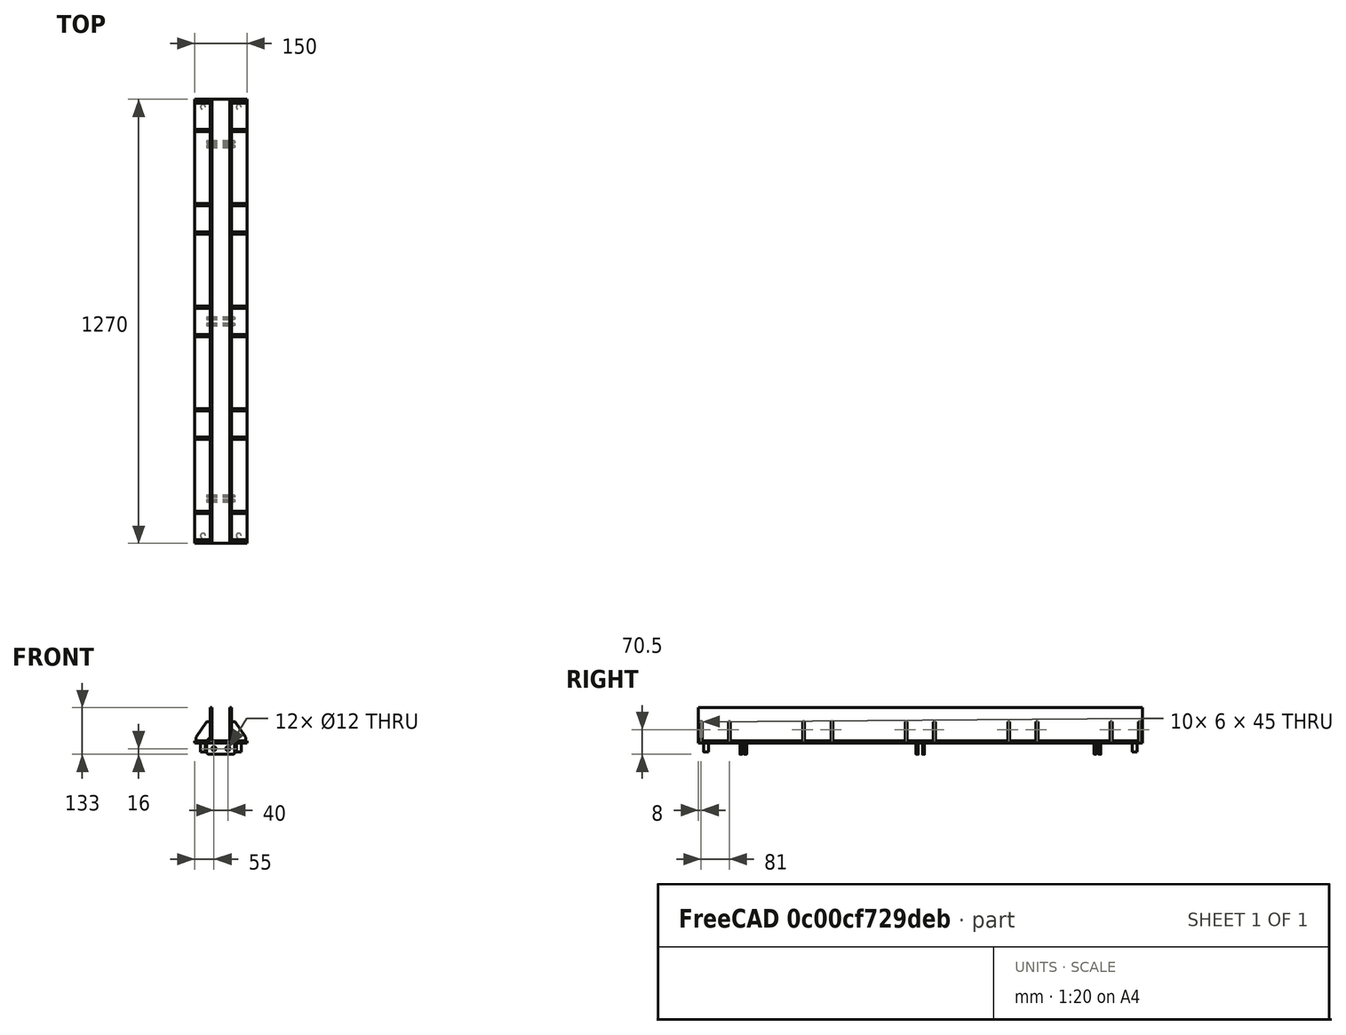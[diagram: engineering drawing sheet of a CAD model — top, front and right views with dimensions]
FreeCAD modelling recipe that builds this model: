
FCSTD DOCUMENT  (FreeCAD 0.21R33771 (Git))
Label: Transom 1270_95_20kN_load
License: All rights reserved
LicenseURL: https://en.wikipedia.org/wiki/All_rights_reserved
objects: Part::FeaturePython×12, Sketcher::SketchObject×3, Fem::ConstraintDisplacement×2, PartDesign::Pad×1, PartDesign::Body×1, Part::Cylinder×1, Part::Compound×1, App::MaterialObjectPython×1, Fem::FemSolverObjectPython×1, Part::MultiFuse×1, Fem::ConstraintForce×1, Fem::FemMeshObjectPython×1, Fem::FemAnalysis×1
note: 19 computed .brp shape members not serialized (recipe doc carries the construction recipe); baked Part::Feature solids carry a one-line shape summary decoded from their .brp

FEATURE [Sketcher::SketchObject] Sketch
  FullyConstrained = true
  MapMode = 5
  Placement = pos=(0,0,0) rot=(1,0,0;1.5708rad)
  sketch-geometry (14):
    g0: LineSegment StartX=0 StartY=0 StartZ=0 EndX=75 EndY=0 EndZ=0
    g1: LineSegment StartX=75 StartY=0 StartZ=0 EndX=75 EndY=6 EndZ=0
    g2: LineSegment StartX=75 StartY=6 StartZ=0 EndX=31 EndY=6 EndZ=0
    g3: LineSegment StartX=31 StartY=6 StartZ=0 EndX=31 EndY=101 EndZ=0
    g4: LineSegment StartX=31 StartY=101 StartZ=0 EndX=25 EndY=101 EndZ=0
    g5: LineSegment StartX=25 StartY=101 StartZ=0 EndX=25 EndY=6 EndZ=0
    g6: LineSegment StartX=25 StartY=6 StartZ=0 EndX=0 EndY=6 EndZ=0
    g7: LineSegment StartX=0 StartY=6 StartZ=0 EndX=-25 EndY=6 EndZ=0
    g8: LineSegment StartX=-25 StartY=6 StartZ=0 EndX=-25 EndY=101 EndZ=0
    g9: LineSegment StartX=-25 StartY=101 StartZ=0 EndX=-31 EndY=101 EndZ=0
    g10: LineSegment StartX=-31 StartY=101 StartZ=0 EndX=-31 EndY=6 EndZ=0
    g11: LineSegment StartX=-31 StartY=6 StartZ=0 EndX=-75 EndY=6 EndZ=0
    g12: LineSegment StartX=-75 StartY=6 StartZ=0 EndX=-75 EndY=0 EndZ=0
    g13: LineSegment StartX=-75 StartY=0 StartZ=0 EndX=0 EndY=0 EndZ=0
  constraints (41):
    c: Coincident(g-1,g0)
    c: PointOnObject(g0,g-1)
    c: Coincident(g0,g1)
    c: Coincident(g1,g2)
    c: Horizontal(g2)
    c: Coincident(g2,g3)
    c: Vertical(g3)
    c: Coincident(g3,g4)
    c: Horizontal(g4)
    c: Coincident(g4,g5)
    c: Vertical(g5)
    c: Coincident(g5,g6)
    c: PointOnObject(g6,g-2)
    c: Horizontal(g6)
    c: DistanceX(g4,g4) = 6
    c: Vertical(g1)
    c: DistanceY(g1,g1) = 6
    c: DistanceY(g0,g6) = 6
    c: DistanceX(g6,g5) = 25
    c: DistanceX(g0,g0) = 75
    c: DistanceY(g3,g3) = 95
    c: Coincident(g6,g7)
    c: Coincident(g7,g8)
    c: Vertical(g8)
    c: Coincident(g8,g9)
    c: Horizontal(g9)
    c: Coincident(g9,g10)
    c: Vertical(g10)
    c: Coincident(g10,g11)
    c: Horizontal(g11)
    c: Coincident(g11,g12)
    c: Coincident(g12,g13)
    c: Coincident(g13,g-1)
    c: Horizontal(g13)
    c: Equal(g5,g10)
    c: Horizontal(g4,g8)
    c: Horizontal(g5,g7)
    c: Vertical(g12)
    c: Equal(g6,g7)
    c: Equal(g2,g11)
    c: Equal(g4,g9)
FEATURE [PartDesign::Pad] Pad
  Direction = (0,-1,2e-16)
  Length = 1270
  Length2 = 10
  Placement = pos=(0,0,0) rot=(1,0,0;1.5708rad)
  Profile = -> Sketch
  ReferenceAxis = -> Sketch [N_Axis]
  Refine = true
  Type = 0
FEATURE [PartDesign::Body] Body
  Group = -> [Sketch,Pad]
  Origin = -> Origin
  Placement = pos=(0,0,0) rot=(0,0,1;3.14159rad)
  Tip = -> Pad
FEATURE [Part::Cylinder] Cylinder
  Angle = 360
  AttacherType = Attacher::AttachEngine3D
  FirstAngle = 0
  Height = 25
  Placement = pos=(51,22,0) rot=(1,0,0;3.14159rad)
  Radius = 7
  SecondAngle = 0
FEATURE [Part::FeaturePython] Array  label="Array_ Transom to Jack Pin"  # Draft array (typed FeaturePython)
  AlwaysSyncPlacement = false
  Angle = 360
  ArrayType = 0
  Axis = (0,0,1)
  Base = -> Cylinder
  Center = (0,0,0)
  Count = 4
  ExpandArray = false
  Fuse = false
  IntervalAxis = (0,0,0)
  IntervalX = (-102,0,0)
  IntervalY = (0,1226,0)
  IntervalZ = (0,0,100)
  NumberCircles = 3
  NumberPolar = 5
  NumberX = 2
  NumberY = 2
  NumberZ = 1
  PlacementList = 4 placements: [(51,22,0),(51,1248,0),(-51,22,0),(-51,1248,0)]
  RadialDistance = 50
  ScaleList = (4) [(1,1,1),(1,1,1),(1,1,1),(1,1,1)]
  Symmetry = 1
  TangentialDistance = 25
FEATURE [Part::FeaturePython] b_Transom_Web_001_  label="Transom Web_Body_001"  # a2plus imported part (geometry in sourceFile) (typed FeaturePython)
  Placement = pos=(31,11,6) rot=(0,0,1;0rad)
  a2p_Version = 0.4.68
  fixedPosition = true
  objectType = a2pPart
  sourceFile = ./Transom Web.FCStd
  sourcePart = Body
  subassemblyImport = false
  timeLastImport = 1.75005e+09
  updateColors = true
FEATURE [Part::FeaturePython] b_Transom_Cleat_001_  label="Transom Cleat_001"  # a2plus imported part (geometry in sourceFile) (typed FeaturePython)
  Placement = pos=(0,125,0) rot=(0,0,1;0rad)
  a2p_Version = 0.4.68
  fixedPosition = true
  objectType = a2pPart
  sourceFile = ./Transom Cleat.FCStd
  subassemblyImport = false
  timeLastImport = 1.75161e+09
  updateColors = true
FEATURE [Part::FeaturePython] b_Transom_Cleat_001_001  label="Transom Cleat_002"  # a2plus imported part (geometry in sourceFile) (typed FeaturePython)
  Placement = pos=(0,138,0) rot=(0,0,1;0rad)
  a2p_Version = 0.4.68
  fixedPosition = false
  objectType = a2pPart
  sourceFile = ./Transom Cleat.FCStd
  subassemblyImport = false
  timeLastImport = 1.75161e+09
  updateColors = true
FEATURE [Part::FeaturePython] b_Transom_Cleat_001_002  label="Transom Cleat_003"  # a2plus imported part (geometry in sourceFile) (typed FeaturePython)
  Placement = pos=(0,1138,0) rot=(0,0,1;0rad)
  a2p_Version = 0.4.68
  fixedPosition = false
  objectType = a2pPart
  sourceFile = ./Transom Cleat.FCStd
  subassemblyImport = false
  timeLastImport = 1.75161e+09
  updateColors = true
FEATURE [Part::FeaturePython] b_Transom_Cleat_001_003  label="Transom Cleat_004"  # a2plus imported part (geometry in sourceFile) (typed FeaturePython)
  Placement = pos=(0,1151,0) rot=(0,0,1;0rad)
  a2p_Version = 0.4.68
  fixedPosition = false
  objectType = a2pPart
  sourceFile = ./Transom Cleat.FCStd
  subassemblyImport = false
  timeLastImport = 1.75161e+09
  updateColors = true
FEATURE [Sketcher::SketchObject] Sketch001
  FullyConstrained = true
  Placement = pos=(0,0,6) rot=(0,0,1;0rad)
  sketch-geometry (40):
    g0: LineSegment StartX=31 StartY=81 StartZ=0 EndX=31 EndY=16 EndZ=0
    g1: LineSegment StartX=31 StartY=16 StartZ=0 EndX=81 EndY=16 EndZ=0
    g2: LineSegment StartX=81 StartY=16 StartZ=0 EndX=81 EndY=81 EndZ=0
    g3: LineSegment StartX=81 StartY=81 StartZ=0 EndX=31 EndY=81 EndZ=0
    g4: LineSegment StartX=31 StartY=667.5 StartZ=0 EndX=31 EndY=602.5 EndZ=0
    g5: LineSegment StartX=31 StartY=602.5 StartZ=0 EndX=81 EndY=602.5 EndZ=0
    g6: LineSegment StartX=81 StartY=602.5 StartZ=0 EndX=81 EndY=667.5 EndZ=0
    g7: LineSegment StartX=81 StartY=667.5 StartZ=0 EndX=31 EndY=667.5 EndZ=0
    g8: LineSegment StartX=31 StartY=1189 StartZ=0 EndX=31 EndY=1254 EndZ=0
    g9: LineSegment StartX=31 StartY=1254 StartZ=0 EndX=81 EndY=1254 EndZ=0
    g10: LineSegment StartX=81 StartY=1254 StartZ=0 EndX=81 EndY=1189 EndZ=0
    g11: LineSegment StartX=81 StartY=1189 StartZ=0 EndX=31 EndY=1189 EndZ=0
    g12: LineSegment StartX=31 StartY=374.25 StartZ=0 EndX=31 EndY=309.25 EndZ=0
    g13: LineSegment StartX=31 StartY=309.25 StartZ=0 EndX=81 EndY=309.25 EndZ=0
    g14: LineSegment StartX=81 StartY=309.25 StartZ=0 EndX=81 EndY=374.25 EndZ=0
    g15: LineSegment StartX=81 StartY=374.25 StartZ=0 EndX=31 EndY=374.25 EndZ=0
    g16: LineSegment StartX=31 StartY=960.75 StartZ=0 EndX=31 EndY=895.75 EndZ=0
    g17: LineSegment StartX=31 StartY=895.75 StartZ=0 EndX=81 EndY=895.75 EndZ=0
    g18: LineSegment StartX=81 StartY=895.75 StartZ=0 EndX=81 EndY=960.75 EndZ=0
    g19: LineSegment StartX=81 StartY=960.75 StartZ=0 EndX=31 EndY=960.75 EndZ=0
    g20: LineSegment StartX=-31 StartY=81 StartZ=0 EndX=-31 EndY=16 EndZ=0
    g21: LineSegment StartX=-31 StartY=16 StartZ=0 EndX=-81 EndY=16 EndZ=0
    g22: LineSegment StartX=-81 StartY=16 StartZ=0 EndX=-81 EndY=81 EndZ=0
    g23: LineSegment StartX=-81 StartY=81 StartZ=0 EndX=-31 EndY=81 EndZ=0
    g24: LineSegment StartX=-31 StartY=667.5 StartZ=0 EndX=-31 EndY=602.5 EndZ=0
    g25: LineSegment StartX=-31 StartY=602.5 StartZ=0 EndX=-81 EndY=602.5 EndZ=0
    g26: LineSegment StartX=-81 StartY=602.5 StartZ=0 EndX=-81 EndY=667.5 EndZ=0
    g27: LineSegment StartX=-81 StartY=667.5 StartZ=0 EndX=-31 EndY=667.5 EndZ=0
    g28: LineSegment StartX=-31 StartY=1189 StartZ=0 EndX=-31 EndY=1254 EndZ=0
    g29: LineSegment StartX=-31 StartY=1254 StartZ=0 EndX=-81 EndY=1254 EndZ=0
    g30: LineSegment StartX=-81 StartY=1254 StartZ=0 EndX=-81 EndY=1189 EndZ=0
    g31: LineSegment StartX=-81 StartY=1189 StartZ=0 EndX=-31 EndY=1189 EndZ=0
    g32: LineSegment StartX=-31 StartY=374.25 StartZ=0 EndX=-31 EndY=309.25 EndZ=0
    g33: LineSegment StartX=-31 StartY=309.25 StartZ=0 EndX=-81 EndY=309.25 EndZ=0
    g34: LineSegment StartX=-81 StartY=309.25 StartZ=0 EndX=-81 EndY=374.25 EndZ=0
    g35: LineSegment StartX=-81 StartY=374.25 StartZ=0 EndX=-31 EndY=374.25 EndZ=0
    g36: LineSegment StartX=-31 StartY=960.75 StartZ=0 EndX=-31 EndY=895.75 EndZ=0
    g37: LineSegment StartX=-31 StartY=895.75 StartZ=0 EndX=-81 EndY=895.75 EndZ=0
    g38: LineSegment StartX=-81 StartY=895.75 StartZ=0 EndX=-81 EndY=960.75 EndZ=0
    g39: LineSegment StartX=-81 StartY=960.75 StartZ=0 EndX=-31 EndY=960.75 EndZ=0
  constraints (120):
    c: Coincident(g0,g1)
    c: Coincident(g1,g2)
    c: Coincident(g2,g3)
    c: Coincident(g3,g0)
    c: Vertical(g0)
    c: Vertical(g2)
    c: Horizontal(g1)
    c: Horizontal(g3)
    c: DistanceY(g2,g2) = 65
    c: DistanceX(g3,g3) = 50
    c: DistanceY(g-1,g0) = 16
    c: DistanceX(g-1,g0) = 31
    c: Coincident(g4,g5)
    c: Coincident(g5,g6)
    c: Coincident(g6,g7)
    c: Coincident(g7,g4)
    c: Vertical(g4)
    c: Vertical(g6)
    c: Horizontal(g5)
    c: Horizontal(g7)
    c: Coincident(g8,g9)
    c: Coincident(g9,g10)
    c: Coincident(g10,g11)
    c: Coincident(g11,g8)
    c: Vertical(g8)
    c: Vertical(g10)
    c: Horizontal(g9)
    c: Horizontal(g11)
    c: Equal(g2,g6)
    c: Equal(g6,g10)
    c: Equal(g1,g5)
    c: Equal(g5,g9)
    c: Vertical(g2,g6)
    c: Vertical(g6,g10)
    c: DistanceY(g2,g5) = 521.5
    c: DistanceY(g6,g9) = 586.5
    c: Coincident(g12,g13)
    c: Coincident(g13,g14)
    c: Coincident(g14,g15)
    c: Coincident(g15,g12)
    c: Vertical(g12)
    c: Vertical(g14)
    c: Horizontal(g13)
    c: Horizontal(g15)
    c: Coincident(g16,g17)
    c: Coincident(g17,g18)
    c: Coincident(g18,g19)
    c: Coincident(g19,g16)
    c: Vertical(g16)
    c: Vertical(g18)
    c: Horizontal(g17)
    c: Horizontal(g19)
    c: Vertical(g0,g12)
    c: Vertical(g12,g16)
    c: Vertical(g2,g13)
    c: Vertical(g13,g17)
    c: Equal(g0,g12)
    c: Equal(g12,g16)
    c: DistanceY(g2,g13) = 228.25
    c: DistanceY(g6,g17) = 228.25
    c: Coincident(g20,g21)
    c: Coincident(g21,g22)
    c: Coincident(g22,g23)
    c: Coincident(g23,g20)
    c: Vertical(g20)
    c: Vertical(g22)
    c: Horizontal(g21)
    c: Horizontal(g23)
    c: Coincident(g24,g25)
    c: Coincident(g25,g26)
    c: Coincident(g26,g27)
    c: Coincident(g27,g24)
    c: Vertical(g24)
    c: Vertical(g26)
    c: Horizontal(g25)
    c: Horizontal(g27)
    c: Coincident(g28,g29)
    c: Coincident(g29,g30)
    c: Coincident(g30,g31)
    c: Coincident(g31,g28)
    c: Vertical(g28)
    c: Vertical(g30)
    c: Horizontal(g29)
    c: Horizontal(g31)
    c: Equal(g22,g26)
    c: Equal(g26,g30)
    c: Equal(g21,g25)
    c: Equal(g25,g29)
    c: Coincident(g32,g33)
    c: Coincident(g33,g34)
    c: Coincident(g34,g35)
    c: Coincident(g35,g32)
    c: Vertical(g32)
    c: Vertical(g34)
    c: Horizontal(g33)
    c: Horizontal(g35)
    c: Coincident(g36,g37)
    c: Coincident(g37,g38)
    c: Coincident(g38,g39)
    c: Coincident(g39,g36)
    c: Vertical(g36)
    c: Vertical(g38)
    c: Horizontal(g37)
    c: Horizontal(g39)
    c: Equal(g20,g32)
    c: Equal(g32,g36)
    c: Horizontal(g32,g12)
    c: Horizontal(g24,g4)
    c: Horizontal(g36,g16)
    c: Horizontal(g28,g8)
    c: Vertical(g21,g33)
    c: Vertical(g33,g25)
    c: Vertical(g25,g37)
    c: Vertical(g37,g30)
    c: Equal(g0,g22)
    c: DistanceY(g-1,g20) = 16
    c: DistanceX(g20,g-1) = 31
    c: Equal(g3,g23)
    c: Equal(g15,g35)
    c: Equal(g19,g39)
FEATURE [Part::FeaturePython] b_Transom_Cleat_001_004  label="Transom Cleat_005"  # a2plus imported part (geometry in sourceFile) (typed FeaturePython)
  Placement = pos=(0,647,0) rot=(0,0,1;0rad)
  a2p_Version = 0.4.68
  fixedPosition = false
  objectType = a2pPart
  sourceFile = ./Transom Cleat.FCStd
  subassemblyImport = false
  timeLastImport = 1.75161e+09
  updateColors = true
FEATURE [Part::FeaturePython] b_Transom_Cleat_001_005  label="Transom Cleat_006"  # a2plus imported part (geometry in sourceFile) (typed FeaturePython)
  Placement = pos=(-4.61864e-06,629,3.05661e-08) rot=(0,0,1;0rad)
  a2p_Version = 0.4.68
  fixedPosition = false
  objectType = a2pPart
  sourceFile = ./Transom Cleat.FCStd
  subassemblyImport = false
  timeLastImport = 1.75161e+09
  updateColors = true
FEATURE [Sketcher::SketchObject] Sketch002
  FullyConstrained = true
  MapMode = 5
  Placement = pos=(0,0,1e-15) rot=(1,0,0;3.14159rad)
  sketch-geometry (12):
    g0: LineSegment StartX=-80 StartY=-55 StartZ=0 EndX=-80 EndY=-75 EndZ=0
    g1: LineSegment StartX=-80 StartY=-75 StartZ=0 EndX=80 EndY=-75 EndZ=0
    g2: LineSegment StartX=80 StartY=-75 StartZ=0 EndX=80 EndY=-55 EndZ=0
    g3: LineSegment StartX=80 StartY=-55 StartZ=0 EndX=-80 EndY=-55 EndZ=0
    g4: LineSegment StartX=-80 StartY=-1195 StartZ=0 EndX=-80 EndY=-1215 EndZ=0
    g5: LineSegment StartX=-80 StartY=-1215 StartZ=0 EndX=80 EndY=-1215 EndZ=0
    g6: LineSegment StartX=80 StartY=-1215 StartZ=0 EndX=80 EndY=-1195 EndZ=0
    g7: LineSegment StartX=80 StartY=-1195 StartZ=0 EndX=-80 EndY=-1195 EndZ=0
    g8: LineSegment StartX=-80 StartY=-629 StartZ=0 EndX=-80 EndY=-641 EndZ=0
    g9: LineSegment StartX=-80 StartY=-641 StartZ=0 EndX=80 EndY=-641 EndZ=0
    g10: LineSegment StartX=80 StartY=-641 StartZ=0 EndX=80 EndY=-629 EndZ=0
    g11: LineSegment StartX=80 StartY=-629 StartZ=0 EndX=-80 EndY=-629 EndZ=0
  constraints (33):
    c: Coincident(g0,g1)
    c: Coincident(g1,g2)
    c: Coincident(g2,g3)
    c: Coincident(g3,g0)
    c: Vertical(g0)
    c: Vertical(g2)
    c: Horizontal(g3)
    c: Distance(g0,g2) = 160
    c: Distance(g1,g3) = 20
    c: Coincident(g4,g5)
    c: Coincident(g5,g6)
    c: Coincident(g6,g7)
    c: Coincident(g7,g4)
    c: Vertical(g4)
    c: Vertical(g6)
    c: Horizontal(g7)
    c: Symmetric(g0,g1,g-2)
    c: DistanceY(g1,g-1) = 75
    c: Equal(g3,g7)
    c: Symmetric(g4,g5,g-2)
    c: DistanceY(g6,g6) = 20
    c: DistanceY(g6,g-1) = 1195
    c: Coincident(g8,g9)
    c: Coincident(g9,g10)
    c: Coincident(g10,g11)
    c: Coincident(g11,g8)
    c: Vertical(g8)
    c: Vertical(g10)
    c: Horizontal(g11)
    c: DistanceY(g10,g10) = 12
    c: DistanceX(g9,g9) = 160
    c: Symmetric(g8,g9,g-2)
    c: DistanceY(g10,g-1) = 629
FEATURE [Part::FeaturePython] b_Transom_Web_Body_001_  label="Transom Web_Body_002"  # a2plus imported part (geometry in sourceFile) (typed FeaturePython)
  Placement = pos=(31,92,6) rot=(0,0,1;0rad)
  a2p_Version = 0.4.68
  fixedPosition = false
  objectType = a2pPart
  sourceFile = ./Transom Web.FCStd
  sourcePart = Body
  subassemblyImport = false
  timeLastImport = 1.75005e+09
  updateColors = true
FEATURE [Part::FeaturePython] b_Transom_Web_Body_001_001  label="Transom Web_Body_003"  # a2plus imported part (geometry in sourceFile) (typed FeaturePython)
  Placement = pos=(-31,5,6) rot=(0,0,1;3.14159rad)
  a2p_Version = 0.4.68
  fixedPosition = false
  objectType = a2pPart
  sourceFile = ./Transom Web.FCStd
  sourcePart = Body
  subassemblyImport = false
  timeLastImport = 1.75005e+09
  updateColors = true
FEATURE [Part::FeaturePython] b_Transom_Web_Body_001_002  label="Transom Web_Body_004"  # a2plus imported part (geometry in sourceFile) (typed FeaturePython)
  Placement = pos=(-31,86,6) rot=(0,0,1;3.14159rad)
  a2p_Version = 0.4.68
  fixedPosition = false
  objectType = a2pPart
  sourceFile = ./Transom Web.FCStd
  sourcePart = Body
  subassemblyImport = false
  timeLastImport = 1.75005e+09
  updateColors = true
FEATURE [Part::Compound] Compound  label="Compound of Webs"
  Links = -> [b_Transom_Web_001_,b_Transom_Web_Body_001_,b_Transom_Web_Body_001_001,b_Transom_Web_Body_001_002]
FEATURE [Part::FeaturePython] Array001  label="Array of Webs"  # Draft array (typed FeaturePython)
  AlwaysSyncPlacement = false
  Angle = 360
  ArrayType = 0
  Axis = (0,0,1)
  Base = -> Compound
  Center = (0,0,0)
  Count = 5
  ExpandArray = false
  Fuse = false
  IntervalAxis = (0,0,0)
  IntervalX = (1270,0,0)
  IntervalY = (0,293.25,0)
  IntervalZ = (0,0,100)
  NumberCircles = 3
  NumberPolar = 5
  NumberX = 1
  NumberY = 5
  NumberZ = 1
  PlacementList = 5 placements: arithmetic series from (0,0,0) step (0,293.25,0) to (0,1173,0)
  RadialDistance = 50
  ScaleList = (5) [(1,1,1),(1,1,1),(1,1,1),(1,1,1),(1,1,1)]
  Symmetry = 1
  TangentialDistance = 25
FEATURE [App::MaterialObjectPython] MaterialSolid  label="steel"  # material (typed FeaturePython)
  Category = 0
  Material = AmbientColor=(0.0020, 0.0020, 0.0020, 1.0),Author=M. Münch,AuthorAndLicense=LGPL-2.0-or-later,CardName=Steel-S235JO,Density=7.8e-06 kg/mm^3,+18 more (map truncated)
  UUID = 5b13e02a-b173-4e2d-95fd-a30d9e0f7cf5
FEATURE [Fem::FemSolverObjectPython] SolverCcxTools  # FEM object (typed FeaturePython)
  AnalysisType = 4
  BeamReducedIntegration = true
  BeamShellResultOutput3D = true
  BucklingFactors = 5
  EigenmodeHighLimit = 1000000
  EigenmodeLowLimit = 0
  EigenmodesCount = 10
  GeometricalNonlinearity = 0
  IterationsControlParameterCutb = 0.25,0.5,0.75,0.85,,,1.5,
  IterationsControlParameterIter = 4,8,9,200,10,400,,200,,
  IterationsControlParameterTimeUse = false
  IterationsMaximum = 2000
  IterationsThermoMechMaximum = 2000
  IterationsUserDefinedIncrementations = false
  IterationsUserDefinedTimeStepLength = false
  MaterialNonlinearity = 0
  MatrixSolverType = 0
  ModelSpace = 0
  OutputFrequency = 1
  SplitInputWriter = true
  ThermoMechSteadyState = true
  ThermoMechType = 0
  TimeEnd = 1
  TimeInitialStep = 0.01
  TimeMaximumStep = 1
  TimeMinimumStep = 1e-05
FEATURE [Part::MultiFuse] Fusion
  Refine = true
  Shapes = -> [Body,Array,Array001,b_Transom_Cleat_001_,b_Transom_Cleat_001_001,b_Transom_Cleat_001_002,b_Transom_Cleat_001_003,b_Transom_Cleat_001_004,b_Transom_Cleat_001_005]
FEATURE [Fem::ConstraintDisplacement] ConstraintDisplacement  label="XYZ"
  NormalDirection = (0,2e-16,-1)
  Normals = (4) [(0,2e-16,-1),(0,2e-16,-1),(0,2e-16,-1),(0,2e-16,-1)]
  Points = (4) [(75,0,0),(25,0,0),(-25,0,0),(-75,0,0)]
  References = -> [Fusion]
  Scale = 13
  hasXFormula = false
  hasYFormula = false
  hasZFormula = false
  rotxFix = false
  rotxFree = true
  rotyFix = false
  rotyFree = true
  rotzFix = false
  rotzFree = true
  useFlowSurfaceForce = false
  xDisplacement = 0
  xFix = false
  xFree = false
  xRotation = 0
  yDisplacement = 0
  yFix = false
  yFree = false
  yRotation = 0
  zDisplacement = 0
  zFix = false
  zFree = false
  zRotation = 0
FEATURE [Fem::ConstraintDisplacement] ConstraintDisplacement001  label="XZ"
  NormalDirection = (0,2e-16,-1)
  Normals = (4) [(0,2e-16,-1),(0,2e-16,-1),(0,2e-16,-1),(0,2e-16,-1)]
  Points = (4) [(75,1270,2.82e-13),(25,1270,2.82e-13),(-25,1270,2.82e-13),(-75,1270,2.82e-13)]
  References = -> [Fusion]
  Scale = 13
  hasXFormula = false
  hasYFormula = false
  hasZFormula = false
  rotxFix = false
  rotxFree = true
  rotyFix = false
  rotyFree = true
  rotzFix = false
  rotzFree = true
  useFlowSurfaceForce = false
  xDisplacement = 0
  xFix = false
  xFree = false
  xRotation = 0
  yDisplacement = 0
  yFix = false
  yFree = true
  yRotation = 0
  zDisplacement = 0
  zFix = false
  zFree = false
  zRotation = 0
FEATURE [Fem::ConstraintForce] ConstraintForce  label="100kN"
  DirectionVector = (0,2e-16,-1)
  Force = 100000
  NormalDirection = (0,-2e-16,1)
  Points = (48) [(31,1270,6),(45.6667,1270,6),(60.3333,1270,6),(75,1270,6),(31,1016,6),(45.6667,1016,6),(60.3333,1016,6),(75,1016,6),(31,762,6),(45.6667,762,6),+38 more]
  References = -> [Fusion]
  Reversed = true
  Scale = 27
FEATURE [Fem::FemMeshObjectPython] FEMMeshGmsh  # FEM object (typed FeaturePython)
  Algorithm2D = 0
  Algorithm3D = 0
  CharacteristicLengthMax = 6
  CharacteristicLengthMin = 0
  CoherenceMesh = true
  ElementDimension = 0
  ElementOrder = 1
  GeometryTolerance = 1e-06
  GroupsOfNodes = false
  HighOrderOptimize = 0
  MeshSizeFromCurvature = 12
  OptimizeNetgen = false
  OptimizeStd = true
  Part = -> Fusion
  RecombinationAlgorithm = 0
  Recombine3DAll = false
  RecombineAll = false
  SecondOrderLinear = false
FEATURE [Fem::FemAnalysis] Analysis
  Group = -> [MaterialSolid,ConstraintDisplacement,ConstraintDisplacement001,ConstraintForce,SolverCcxTools,FEMMeshGmsh]
